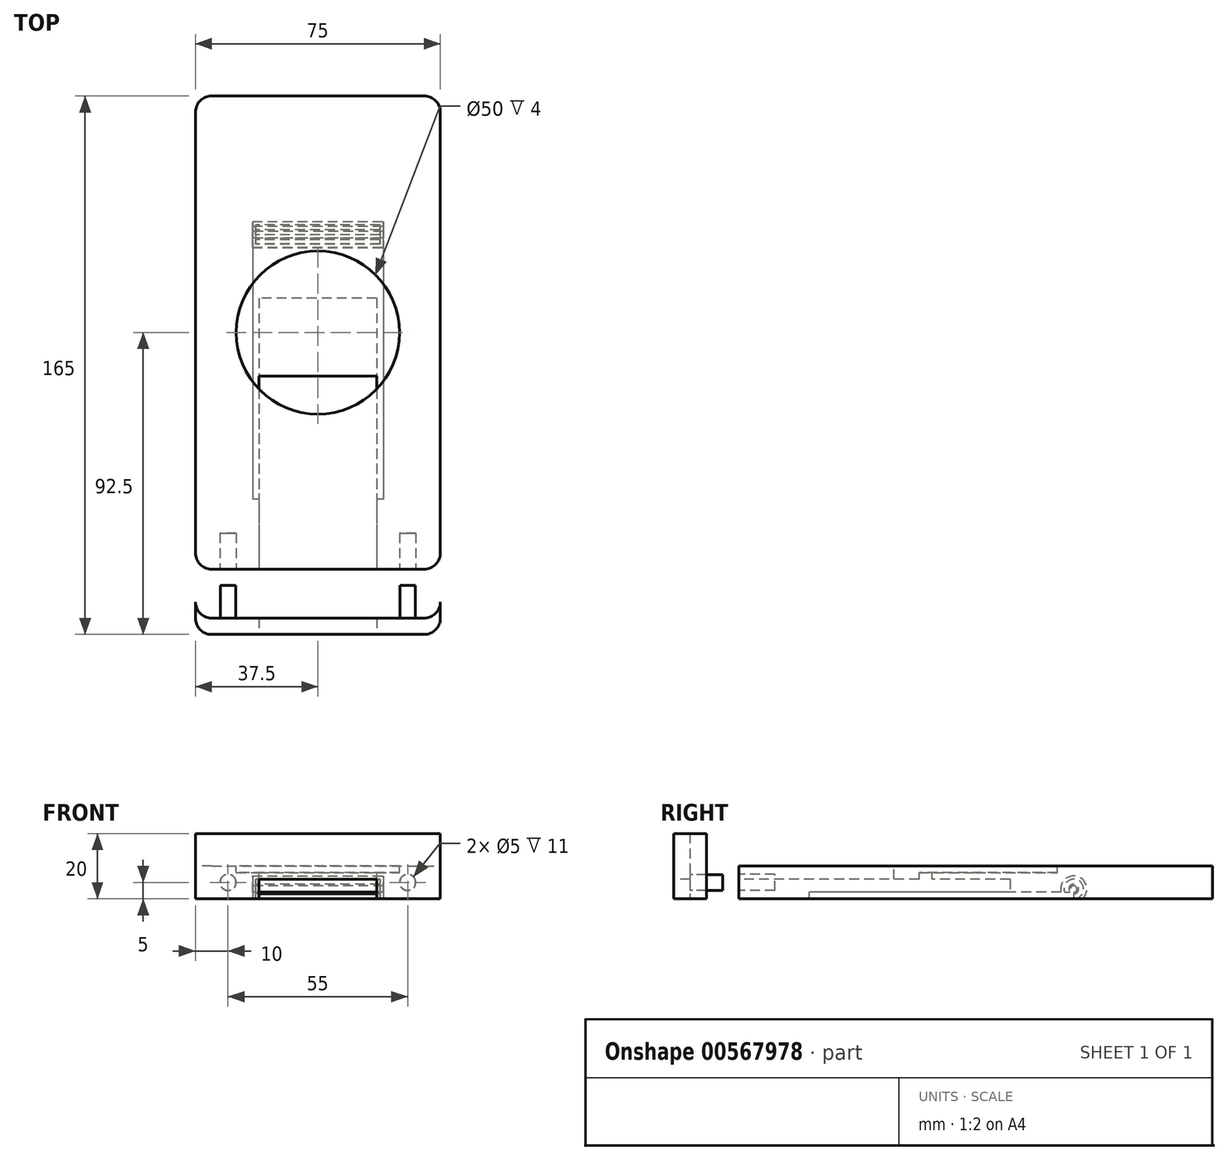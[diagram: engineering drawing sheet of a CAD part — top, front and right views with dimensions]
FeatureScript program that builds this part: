
annotation { "Feature Type Name" : "Feature", "Feature Type Description" : "" }
export const myFeature = defineFeature(function(context is Context, id is Id, definition is map)
    precondition{}
    {
        {
            var Q0;
            Q0=qCreatedBy(makeId("Top.planeOp"),FACE);
            var sketch = newSketch(context, id + "F0", { "sketchPlane" : qUnion([Q0])});
            skLineSegment(sketch, "E0.bottom", {"start": v(-32.5, 72.5) * mm, "end": v(32.5, 72.5) * mm});
            skLineSegment(sketch, "E0.top", {"start": v(-32.5, -72.5) * mm, "end": v(32.5, -72.5) * mm});
            skLineSegment(sketch, "E0.left", {"start": v(-37.5, 67.5) * mm, "end": v(-37.5, -67.5) * mm});
            skLineSegment(sketch, "E0.right", {"start": v(37.5, 67.5) * mm, "end": v(37.5, -67.5) * mm});
            skLineSegment(sketch, "E1", {"start": v(-37.5, 72.5) * mm, "end": v(0, 0) * mm, "construction": true});
            skLineSegment(sketch, "E2", {"start": v(0, 0) * mm, "end": v(-37.5, -72.5) * mm, "construction": true});
            skLineSegment(sketch, "E3", {"start": v(37.5, -72.5) * mm, "end": v(0, 0) * mm, "construction": true});
            skPoint(sketch, "E4.visualSharp", {"position": v(-37.5, 72.5) * mm});
            skArc(sketch, "E4.filletArc", {"start": v(-32.5, 72.5) * mm, "mid": v(-36.04, 71.04) * mm, "end": v(-37.5, 67.5) * mm});
            skPoint(sketch, "E5.visualSharp", {"position": v(37.5, 72.5) * mm});
            skArc(sketch, "E5.filletArc", {"start": v(37.5, 67.5) * mm, "mid": v(36.04, 71.04) * mm, "end": v(32.5, 72.5) * mm});
            skPoint(sketch, "E6.visualSharp", {"position": v(37.5, -72.5) * mm});
            skLineSegment(sketch, "E6.filletArc", {"start": v(37.5, -72.5) * mm, "end": v(37.5, -72.5) * mm});
            skPoint(sketch, "E7.visualSharp", {"position": v(-37.5, -72.5) * mm});
            skArc(sketch, "E7.filletArc", {"start": v(-37.5, -67.5) * mm, "mid": v(-36.04, -71.04) * mm, "end": v(-32.5, -72.5) * mm});
            skArc(sketch, "E8.filletArc", {"start": v(32.5, -72.5) * mm, "mid": v(36.04, -71.04) * mm, "end": v(37.5, -67.5) * mm});
            skSolve(sketch);
        }
        {
            var Q0;
            Q0 = qSketchRegion(id + "F0", true);
            extrude(context, id + "F1", {"entities" : qUnion([Q0]), "depth" : 10 * mm, "offsetDistance" : 25 * mm});
        }
        {
            var Q0;
            Q0=makeQuery(id+"F1.opExtrude","CAP_FACE",FACE,{"disambiguationData":[OSD([sQuery(id+"F0.wireOp",EDGE,"E0.bottom"),sQuery(id+"F0.wireOp",EDGE,"E0.top"),sQuery(id+"F0.wireOp",EDGE,"E0.left"),sQuery(id+"F0.wireOp",EDGE,"E0.right")])],"isStart":false});
            var sketch = newSketch(context, id + "F2", { "sketchPlane" : qUnion([Q0])});
            skCircle(sketch, "E9", {"center": v(0, 0) * mm, "radius": 25 * mm});
            skSolve(sketch);
        }
        {
            var Q0;
            Q0 = qSketchRegion(id + "F2", true);
            extrude(context, id + "F3", {"entities" : qUnion([Q0]), "operationType" : NewBodyOperationType.REMOVE, "oppositeDirection" : true, "depth" : 2 * mm, "offsetDistance" : 25 * mm});
        }
        {
            var Q0;
            Q0=makeQuery(id+"F1.opExtrude","CAP_FACE",FACE,{"disambiguationData":[OSD([sQuery(id+"F0.wireOp",EDGE,"E0.bottom"),sQuery(id+"F0.wireOp",EDGE,"E0.top"),sQuery(id+"F0.wireOp",EDGE,"E0.left"),sQuery(id+"F0.wireOp",EDGE,"E0.right")])],"isStart":true});
            var sketch = newSketch(context, id + "F4", { "sketchPlane" : qUnion([Q0])});
            skLineSegment(sketch, "E10", {"start": v(0, 0) * mm, "end": v(0, -30) * mm, "construction": true});
            skPoint(sketch, "E10.endSnap0", {"position": v(0, -72.5) * mm});
            skLineSegment(sketch, "E11", {"start": v(0, -30) * mm, "end": v(-20, -30) * mm});
            skLineSegment(sketch, "E12", {"start": v(0, -30) * mm, "end": v(20, -30) * mm});
            skSolve(sketch);
        }
        {
            var Q0;
            Q0=qCreatedBy(makeId("Right.planeOp"),FACE);
            var sketch = newSketch(context, id + "F5", { "sketchPlane" : qUnion([Q0])});
            skCircle(sketch, "E13", {"center": v(30, 3) * mm, "radius": 4 * mm});
            skLineSegment(sketch, "E14", {"start": v(30, 3) * mm, "end": v(30, 0) * mm, "construction": true});
            skCircle(sketch, "E15", {"center": v(30, 3) * mm, "radius": 3 * mm, "construction": true});
            skCircle(sketch, "E16", {"center": v(30, 3) * mm, "radius": 1.5 * mm, "construction": true});
            skCircle(sketch, "E17", {"center": v(30, 3) * mm, "radius": 1 * mm, "construction": true});
            skLineSegment(sketch, "E18", {"start": v(32.65, 0) * mm, "end": v(33, 3) * mm, "construction": true});
            skLineSegment(sketch, "E19", {"start": v(33, 3) * mm, "end": v(30, 3) * mm, "construction": true});
            skSolve(sketch);
        }
        {
            var Q0;
            Q0 = qSketchRegion(id + "F5", true);
            var Q1;
            Q1=sQuery(id+"F4.wireOp",VERTEX,"E11.end");
            var Q2;
            Q2=sQuery(id+"F4.wireOp",VERTEX,"E12.end");
            extrude(context, id + "F6", {"entities" : qUnion([Q0]), "operationType" : NewBodyOperationType.REMOVE, "endBound" : BoundingType.UP_TO_VERTEX, "oppositeDirection" : true, "depth" : 25 * mm, "endBoundEntityVertex" : qUnion([Q1]), "offsetDistance" : 25 * mm, "hasSecondDirection" : true, "secondDirectionBound" : SecondDirectionBoundingType.UP_TO_VERTEX, "secondDirectionOppositeDirection" : false, "secondDirectionDepth" : 25 * mm, "secondDirectionBoundEntityVertex" : qUnion([Q2])});
        }
        {
            var Q0;
            Q0=qCreatedBy(makeId("Right.planeOp"),FACE);
            var sketch = newSketch(context, id + "F7", { "sketchPlane" : qUnion([Q0])});
            skCircle(sketch, "E20", {"center": v(30, 3) * mm, "radius": 1 * mm});
            skLineSegment(sketch, "E21", {"start": v(30, 3) * mm, "end": v(30, 0) * mm, "construction": true});
            skSolve(sketch);
        }
        {
            var Q0;
            Q0 = qSketchRegion(id + "F7", true);
            extrude(context, id + "F8", {"entities" : qUnion([Q0]), "operationType" : NewBodyOperationType.ADD, "depth" : 25 * mm, "offsetDistance" : 25 * mm, "hasSecondDirection" : true, "secondDirectionOppositeDirection" : true, "secondDirectionDepth" : 25 * mm});
        }
        {
            var Q0;
            Q0=qCreatedBy(makeId("Right.planeOp"),FACE);
            var sketch = newSketch(context, id + "F9", { "sketchPlane" : qUnion([Q0])});
            skCircle(sketch, "E22", {"center": v(30, 3) * mm, "radius": 3 * mm});
            skCircle(sketch, "E23", {"center": v(30, 3) * mm, "radius": 1.5 * mm});
            skLineSegment(sketch, "E24", {"start": v(30, 3) * mm, "end": v(30, 0) * mm, "construction": true});
            skSolve(sketch);
        }
        {
            var Q0;
            Q0 = qSketchRegion(id + "F9", true);
            extrude(context, id + "F10", {"entities" : qUnion([Q0]), "depth" : 19 * mm, "offsetDistance" : 25 * mm, "hasSecondDirection" : true, "secondDirectionOppositeDirection" : true, "secondDirectionDepth" : 19 * mm});
        }
        {
            var Q0;
            Q0=qCreatedBy(makeId("Right.planeOp"),FACE);
            var sketch = newSketch(context, id + "F11", { "sketchPlane" : qUnion([Q0])});
            skLineSegment(sketch, "E25.bottom", {"start": v(30, 0) * mm, "end": v(-50, 0) * mm});
            skLineSegment(sketch, "E25.top", {"start": v(30, 1.5) * mm, "end": v(-50, 1.5) * mm});
            skLineSegment(sketch, "E25.left", {"start": v(30, 0) * mm, "end": v(30, 1.5) * mm});
            skLineSegment(sketch, "E25.right", {"start": v(-50, 0) * mm, "end": v(-50, 1.5) * mm});
            skSolve(sketch);
        }
        {
            var Q0;
            Q0 = qSketchRegion(id + "F11", true);
            extrude(context, id + "F12", {"entities" : qUnion([Q0]), "operationType" : NewBodyOperationType.ADD, "depth" : 19 * mm, "offsetDistance" : 25 * mm, "hasSecondDirection" : true, "secondDirectionOppositeDirection" : true, "secondDirectionDepth" : 19 * mm});
        }
        {
            var Q0;
            Q0=makeQuery(id+"F4.imprint","IMPRINT",FACE,{"disambiguationData":[TD([[makeQuery(id+"F4.imprint","IMPRINT",EDGE,{"derivedFrom":makeQuery(id+"F1.opExtrude","CAP_EDGE",EDGE,{"disambiguationData":[OSD([sQuery(id+"F0.wireOp",EDGE,"E0.bottom")])],"isStart":true})}),1.0]])]});
            var sketch = newSketch(context, id + "F13", { "sketchPlane" : qUnion([Q0])});
            skLineSegment(sketch, "E26.bottom", {"start": v(20, -30) * mm, "end": v(-20, -30) * mm});
            skLineSegment(sketch, "E26.top", {"start": v(20, 51) * mm, "end": v(-20, 51) * mm});
            skLineSegment(sketch, "E26.left", {"start": v(20, -30) * mm, "end": v(20, 51) * mm});
            skLineSegment(sketch, "E26.right", {"start": v(-20, -30) * mm, "end": v(-20, 51) * mm});
            skSolve(sketch);
        }
        {
            var Q0;
            Q0 = qSketchRegion(id + "F13", true);
            extrude(context, id + "F14", {"entities" : qUnion([Q0]), "operationType" : NewBodyOperationType.REMOVE, "oppositeDirection" : true, "depth" : 2 * mm, "offsetDistance" : 25 * mm});
        }
        {
            var Q0;
            Q0=makeQuery(id+"F3.boolean.opBoolean","COPY",FACE,{"derivedFrom":makeQuery(id+"F3.opExtrude","CAP_FACE",FACE,{"disambiguationData":[OSD([sQuery(id+"F2.wireOp",EDGE,"E9")])],"isStart":false})});
            var sketch = newSketch(context, id + "F15", { "sketchPlane" : qUnion([Q0])});
            skLineSegment(sketch, "E27", {"start": v(-18, -13.35) * mm, "end": v(18, -13.35) * mm});
            skArc(sketch, "E28.0", {"start": v(-21.14, -13.35) * mm, "mid": v(0, -25) * mm, "end": v(21.14, -13.35) * mm});
            skLineSegment(sketch, "E29", {"start": v(-18, -17.35) * mm, "end": v(18, -17.35) * mm, "construction": true});
            skLineSegment(sketch, "E30", {"start": v(-18, -17.35) * mm, "end": v(-18, -13.35) * mm});
            skLineSegment(sketch, "E31", {"start": v(18, -17.35) * mm, "end": v(18, -13.35) * mm});
            skSolve(sketch);
        }
        {
            var Q0;
            Q0 = qSketchRegion(id + "F15", true);
            extrude(context, id + "F16", {"entities" : qUnion([Q0]), "operationType" : NewBodyOperationType.REMOVE, "oppositeDirection" : true, "depth" : 20 * mm, "offsetDistance" : 25 * mm});
        }
        {
            var Q0;
            Q0=makeQuery(id+"F4.imprint","IMPRINT",FACE,{"disambiguationData":[TD([[makeQuery(id+"F4.imprint","IMPRINT",EDGE,{"derivedFrom":makeQuery(id+"F1.opExtrude","CAP_EDGE",EDGE,{"disambiguationData":[OSD([sQuery(id+"F0.wireOp",EDGE,"E0.bottom")])],"isStart":true})}),1.0]])]});
            var sketch = newSketch(context, id + "F17", { "sketchPlane" : qUnion([Q0])});
            skLineSegment(sketch, "E32.bottom", {"start": v(18, -10.5) * mm, "end": v(-18, -10.5) * mm});
            skLineSegment(sketch, "E32.top", {"start": v(18, 79.5) * mm, "end": v(-18, 79.5) * mm});
            skLineSegment(sketch, "E32.left", {"start": v(18, -10.5) * mm, "end": v(18, 79.5) * mm});
            skLineSegment(sketch, "E32.right", {"start": v(-18, -10.5) * mm, "end": v(-18, 79.5) * mm});
            skLineSegment(sketch, "E33", {"start": v(0, 72.5) * mm, "end": v(0, 52.5) * mm, "construction": true});
            skLineSegment(sketch, "E34", {"start": v(0, 52.5) * mm, "end": v(0, 20.5) * mm, "construction": true});
            skLineSegment(sketch, "E35", {"start": v(0, 20.5) * mm, "end": v(0, -10.5) * mm, "construction": true});
            skLineSegment(sketch, "E36", {"start": v(0, 39.5) * mm, "end": v(0, 72.5) * mm, "construction": true});
            skSolve(sketch);
        }
        {
            var Q0;
            Q0 = qSketchRegion(id + "F17", true);
            extrude(context, id + "F18", {"entities" : qUnion([Q0]), "operationType" : NewBodyOperationType.REMOVE, "oppositeDirection" : true, "depth" : 6 * mm, "offsetDistance" : 25 * mm});
        }
        {
            var Q0;
            Q0=qCreatedBy(makeId("Top.planeOp"),FACE);
            var sketch = newSketch(context, id + "F19", { "sketchPlane" : qUnion([Q0])});
            skLineSegment(sketch, "E37.bottom", {"start": v(-32.5, -87.5) * mm, "end": v(32.5, -87.5) * mm});
            skLineSegment(sketch, "E37.top", {"start": v(-32.5, -92.5) * mm, "end": v(32.5, -92.5) * mm});
            skLineSegment(sketch, "E37.left", {"start": v(-37.5, -87.5) * mm, "end": v(-37.5, -87.5) * mm});
            skLineSegment(sketch, "E37.right", {"start": v(37.5, -87.5) * mm, "end": v(37.5, -87.5) * mm});
            skPoint(sketch, "E38.visualSharp", {"position": v(-37.5, -92.5) * mm});
            skArc(sketch, "E38.filletArc", {"start": v(-37.5, -87.5) * mm, "mid": v(-36.04, -91.04) * mm, "end": v(-32.5, -92.5) * mm});
            skPoint(sketch, "E39.visualSharp", {"position": v(37.5, -92.5) * mm});
            skArc(sketch, "E39.filletArc", {"start": v(32.5, -92.5) * mm, "mid": v(36.04, -91.04) * mm, "end": v(37.5, -87.5) * mm});
            skLineSegment(sketch, "E40", {"start": v(32.5, -87.5) * mm, "end": v(32.5, -82.5) * mm, "construction": true});
            skArc(sketch, "E41", {"start": v(32.5, -87.5) * mm, "mid": v(36.04, -86.04) * mm, "end": v(37.5, -82.5) * mm});
            skArc(sketch, "E42", {"start": v(-37.5, -82.5) * mm, "mid": v(-36.04, -86.04) * mm, "end": v(-32.5, -87.5) * mm});
            skLineSegment(sketch, "E43", {"start": v(-37.5, -87.5) * mm, "end": v(-37.5, -82.5) * mm});
            skLineSegment(sketch, "E44", {"start": v(37.5, -87.5) * mm, "end": v(37.5, -82.5) * mm});
            skSolve(sketch);
        }
        {
            var Q0;
            Q0 = qSketchRegion(id + "F19", true);
            extrude(context, id + "F20", {"entities" : qUnion([Q0]), "depth" : 20 * mm, "offsetDistance" : 25 * mm});
        }
        {
            var Q0;
            Q0=makeQuery(id+"F20.opExtrude","SWEPT_FACE",FACE,{"disambiguationData":[OSD([sQuery(id+"F19.wireOp",EDGE,"E37.bottom")])]});
            var sketch = newSketch(context, id + "F21", { "sketchPlane" : qUnion([Q0])});
            skCircle(sketch, "E45", {"center": v(27.5, 5) * mm, "radius": 2.4 * mm});
            skCircle(sketch, "E46.MirrorC", {"center": v(-27.5, 5) * mm, "radius": 2.4 * mm});
            skSolve(sketch);
        }
        {
            var Q0;
            Q0 = qSketchRegion(id + "F21", true);
            extrude(context, id + "F22", {"entities" : qUnion([Q0]), "operationType" : NewBodyOperationType.ADD, "depth" : 10 * mm, "offsetDistance" : 25 * mm});
        }
        {
            var Q0;
            Q0=makeQuery(id+"F1.opExtrude","SWEPT_FACE",FACE,{"disambiguationData":[OSD([sQuery(id+"F0.wireOp",EDGE,"E0.top")])]});
            var sketch = newSketch(context, id + "F23", { "sketchPlane" : qUnion([Q0])});
            skCircle(sketch, "E47", {"center": v(27.5, 5) * mm, "radius": 2.5 * mm});
            skCircle(sketch, "E48.MirrorC", {"center": v(-27.5, 5) * mm, "radius": 2.5 * mm});
            skSolve(sketch);
        }
        {
            var Q0;
            Q0 = qSketchRegion(id + "F23", true);
            extrude(context, id + "F24", {"entities" : qUnion([Q0]), "operationType" : NewBodyOperationType.REMOVE, "oppositeDirection" : true, "depth" : 11 * mm, "offsetDistance" : 25 * mm});
        }
        {
            var Q0;
            Q0=makeQuery(id+"F20.opExtrude","CAP_FACE",FACE,{"disambiguationData":[OSD([sQuery(id+"F19.wireOp",EDGE,"E37.bottom"),sQuery(id+"F19.wireOp",EDGE,"E37.top"),sQuery(id+"F19.wireOp",EDGE,"E38.filletArc"),sQuery(id+"F19.wireOp",EDGE,"E39.filletArc"),sQuery(id+"F19.wireOp",EDGE,"E41"),sQuery(id+"F19.wireOp",EDGE,"E42"),sQuery(id+"F19.wireOp",EDGE,"E43"),sQuery(id+"F19.wireOp",EDGE,"E44")])],"isStart":true});
            var sketch = newSketch(context, id + "F25", { "sketchPlane" : qUnion([Q0])});
            skLineSegment(sketch, "E49.bottom", {"start": v(18, 81.18) * mm, "end": v(-18, 81.18) * mm});
            skLineSegment(sketch, "E49.top", {"start": v(18, 105.32) * mm, "end": v(-18, 105.32) * mm});
            skLineSegment(sketch, "E49.left", {"start": v(18, 81.18) * mm, "end": v(18, 105.32) * mm});
            skLineSegment(sketch, "E49.right", {"start": v(-18, 81.18) * mm, "end": v(-18, 105.32) * mm});
            skSolve(sketch);
        }
        {
            var Q0;
            Q0 = qSketchRegion(id + "F25", true);
            extrude(context, id + "F26", {"entities" : qUnion([Q0]), "operationType" : NewBodyOperationType.REMOVE, "oppositeDirection" : true, "depth" : 6 * mm, "offsetDistance" : 25 * mm});
        }
    });
